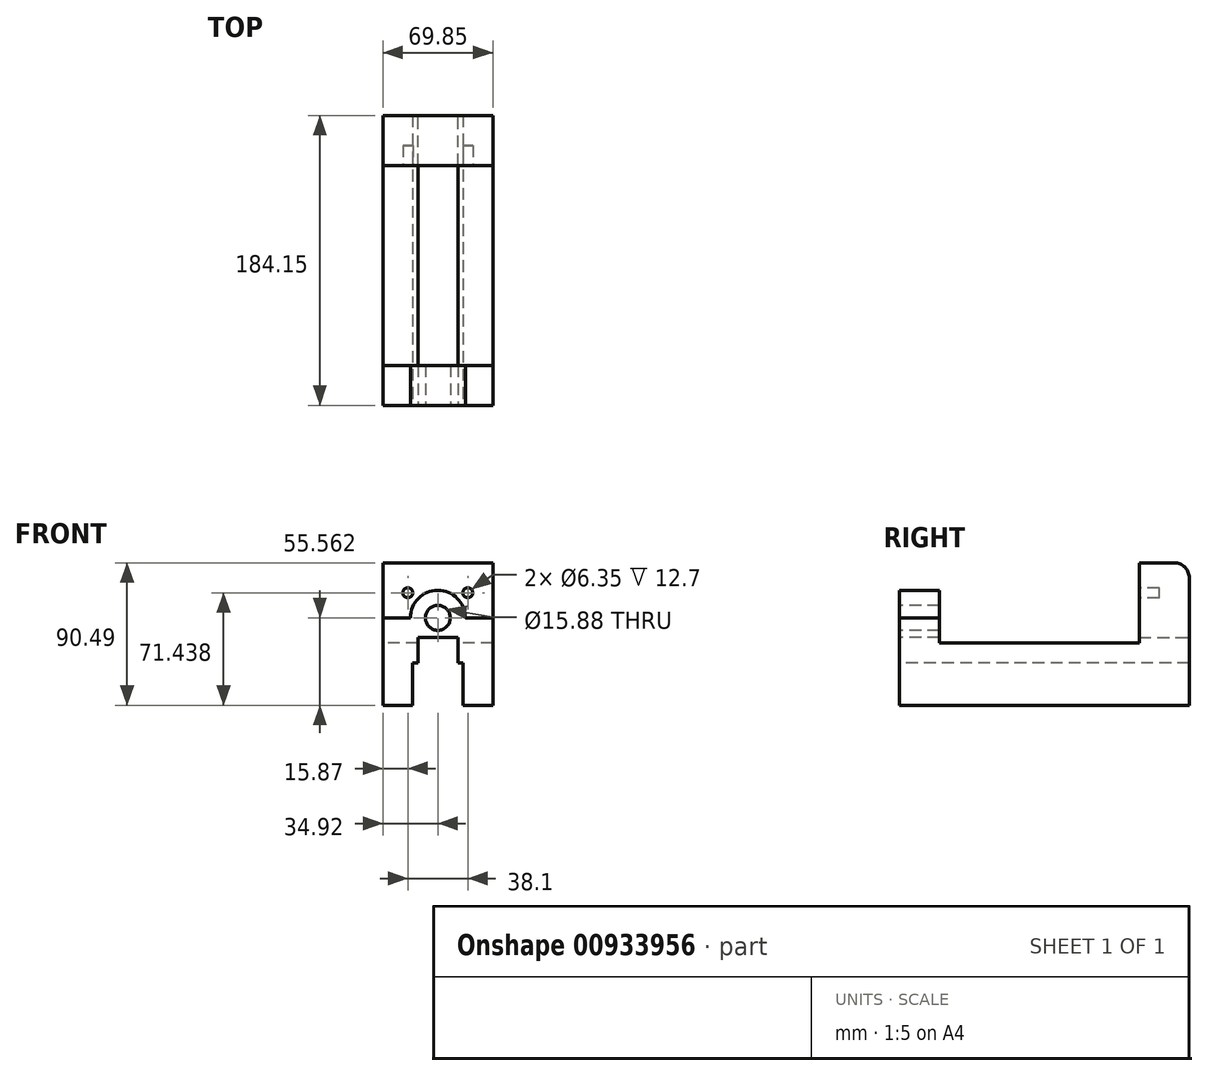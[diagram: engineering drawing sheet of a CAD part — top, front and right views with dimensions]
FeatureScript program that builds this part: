
annotation { "Feature Type Name" : "Feature", "Feature Type Description" : "" }
export const myFeature = defineFeature(function(context is Context, id is Id, definition is map)
    precondition{}
    {
        {
            var Q0;
            Q0=qCreatedBy(makeId("Front.planeOp"),FACE);
            var sketch = newSketch(context, id + "F0", { "sketchPlane" : qUnion([Q0])});
            skLineSegment(sketch, "E0", {"start": v(-27.11, 0) * mm, "end": v(42.74, 0) * mm});
            skLineSegment(sketch, "E1", {"start": v(42.74, 0) * mm, "end": v(42.74, 55.56) * mm});
            skLineSegment(sketch, "E2", {"start": v(42.74, 55.56) * mm, "end": v(-27.11, 55.56) * mm});
            skLineSegment(sketch, "E3", {"start": v(-27.11, 55.56) * mm, "end": v(-27.11, 0) * mm});
            skSolve(sketch);
        }
        {
            var Q0;
            Q0=makeQuery(id+"F0.imprint","IMPRINT",FACE,{"disambiguationData":[TD([[makeQuery(id+"F0.imprint","IMPRINT",EDGE,{"derivedFrom":sQuery(id+"F0.wireOp",EDGE,"E0")}),1.0]])]});
            extrude(context, id + "F1", {"entities" : qUnion([Q0]), "depth" : 25.4 * mm, "offsetDistance" : 25.4 * mm});
        }
        {
            var Q0;
            Q0=makeQuery(id+"F1.opExtrude","CAP_FACE",FACE,{"disambiguationData":[OSD([sQuery(id+"F0.wireOp",EDGE,"E0"),sQuery(id+"F0.wireOp",EDGE,"E1"),sQuery(id+"F0.wireOp",EDGE,"E2"),sQuery(id+"F0.wireOp",EDGE,"E3")])],"isStart":false});
            var sketch = newSketch(context, id + "F2", { "sketchPlane" : qUnion([Q0])});
            skCircle(sketch, "E4", {"center": v(7.81, 55.56) * mm, "radius": 17.46 * mm});
            skSolve(sketch);
        }
        {
            var Q0;
            {var subQ0=sQuery(id+"F2.wireOp",EDGE,"E4");var subQ1=makeQuery(id+"F1.opExtrude","CAP_EDGE",EDGE,{"disambiguationData":[OSD([sQuery(id+"F0.wireOp",EDGE,"E2")])],"isStart":false});var subQ2=makeQuery(id+"F2.imprint","INTERSECT",VERTEX,{"disambiguationData":[OD(0.0)],"derivedFrom":[subQ1,subQ0]});Q0=makeQuery(id+"F2.imprint","IMPRINT",FACE,{"disambiguationData":[TD([[makeQuery(id+"F2.imprint","IMPRINT",EDGE,{"disambiguationData":[TD([[subQ2,-1.0]])],"derivedFrom":subQ0}),1.0]])]});}
            extrude(context, id + "F3", {"entities" : qUnion([Q0]), "operationType" : NewBodyOperationType.ADD, "oppositeDirection" : true, "depth" : 25.4 * mm, "offsetDistance" : 25.4 * mm});
        }
        {
            var Q0;
            {var subQ0=sQuery(id+"F0.wireOp",EDGE,"E2");Q0=makeQuery(id+"F3.boolean.opBoolean","MERGE",FACE,{"derivedFrom":[makeQuery(id+"F1.opExtrude","CAP_FACE",FACE,{"disambiguationData":[OSD([sQuery(id+"F0.wireOp",EDGE,"E0"),sQuery(id+"F0.wireOp",EDGE,"E1"),subQ0,sQuery(id+"F0.wireOp",EDGE,"E3")])],"isStart":false}),makeQuery(id+"F3.opExtrude","CAP_FACE",FACE,{"disambiguationData":[OSD([subQ0,sQuery(id+"F2.wireOp",EDGE,"E4")])],"isStart":true})]});}
            var sketch = newSketch(context, id + "F4", { "sketchPlane" : qUnion([Q0])});
            skCircle(sketch, "E5", {"center": v(7.81, 55.56) * mm, "radius": 7.94 * mm});
            skSolve(sketch);
        }
        {
            var Q0;
            Q0=makeQuery(id+"F4.imprint","IMPRINT",FACE,{"disambiguationData":[TD([[makeQuery(id+"F4.imprint","IMPRINT",EDGE,{"derivedFrom":sQuery(id+"F4.wireOp",EDGE,"E5")}),1.0]])]});
            extrude(context, id + "F5", {"entities" : qUnion([Q0]), "operationType" : NewBodyOperationType.REMOVE, "oppositeDirection" : true, "depth" : 25.4 * mm, "offsetDistance" : 25.4 * mm});
        }
        {
            var Q0;
            {var subQ0=sQuery(id+"F0.wireOp",EDGE,"E2");Q0=makeQuery(id+"F3.boolean.opBoolean","MERGE",FACE,{"derivedFrom":[makeQuery(id+"F1.opExtrude","CAP_FACE",FACE,{"disambiguationData":[OSD([sQuery(id+"F0.wireOp",EDGE,"E0"),sQuery(id+"F0.wireOp",EDGE,"E1"),subQ0,sQuery(id+"F0.wireOp",EDGE,"E3")])],"isStart":true}),makeQuery(id+"F3.opExtrude","CAP_FACE",FACE,{"disambiguationData":[OSD([subQ0,sQuery(id+"F2.wireOp",EDGE,"E4")])],"isStart":false})]});}
            var sketch = newSketch(context, id + "F6", { "sketchPlane" : qUnion([Q0])});
            skLineSegment(sketch, "E6", {"start": v(-42.74, 0) * mm, "end": v(-42.74, 39.69) * mm});
            skLineSegment(sketch, "E7", {"start": v(-42.74, 39.69) * mm, "end": v(27.11, 39.69) * mm});
            skLineSegment(sketch, "E8", {"start": v(27.11, 39.69) * mm, "end": v(27.11, 0) * mm});
            skLineSegment(sketch, "E9", {"start": v(27.11, 0) * mm, "end": v(-42.74, 0) * mm});
            skSolve(sketch);
        }
        {
            var Q0;
            Q0=makeQuery(id+"F6.imprint","IMPRINT",FACE,{"disambiguationData":[TD([[makeQuery(id+"F6.imprint","IMPRINT",EDGE,{"derivedFrom":sQuery(id+"F6.wireOp",EDGE,"E6")}),-1.0]])]});
            extrude(context, id + "F7", {"entities" : qUnion([Q0]), "operationType" : NewBodyOperationType.ADD, "depth" : 127 * mm, "offsetDistance" : 25.4 * mm});
        }
        {
            var Q0;
            Q0=makeQuery(id+"F7.opExtrude","CAP_FACE",FACE,{"disambiguationData":[OSD([sQuery(id+"F6.wireOp",EDGE,"E6"),sQuery(id+"F6.wireOp",EDGE,"E7"),sQuery(id+"F6.wireOp",EDGE,"E8"),sQuery(id+"F6.wireOp",EDGE,"E9")])],"isStart":false});
            var sketch = newSketch(context, id + "F8", { "sketchPlane" : qUnion([Q0])});
            skLineSegment(sketch, "E10", {"start": v(-42.74, 0) * mm, "end": v(-42.74, 90.49) * mm});
            skLineSegment(sketch, "E11", {"start": v(-42.74, 90.49) * mm, "end": v(27.11, 90.49) * mm});
            skLineSegment(sketch, "E12", {"start": v(27.11, 90.49) * mm, "end": v(27.11, 0) * mm});
            skLineSegment(sketch, "E13", {"start": v(27.11, 0) * mm, "end": v(-42.74, 0) * mm});
            skSolve(sketch);
        }
        {
            var Q0;
            {var subQ2=sQuery(id+"F8.wireOp",EDGE,"E11");Q0=makeQuery(id+"F8.imprint","IMPRINT",FACE,{"disambiguationData":[TD([[makeQuery(id+"F8.imprint","IMPRINT",EDGE,{"derivedFrom":subQ2}),-1.0]])]});}
            var Q1;
            {var subQ0=sQuery(id+"F8.wireOp",EDGE,"E13");Q1=makeQuery(id+"F8.imprint","IMPRINT",FACE,{"disambiguationData":[TD([[makeQuery(id+"F8.imprint","IMPRINT",EDGE,{"derivedFrom":subQ0}),-1.0]])]});}
            extrude(context, id + "F9", {"entities" : qUnion([Q0, Q1]), "operationType" : NewBodyOperationType.ADD, "depth" : 31.75 * mm, "offsetDistance" : 25.4 * mm});
        }
        {
            var Q0;
            Q0=makeQuery(id+"F9.opExtrude","CAP_EDGE",EDGE,{"disambiguationData":[OSD([sQuery(id+"F8.wireOp",EDGE,"E11")])],"isStart":false});
            fillet(context, id + "F10", {"entities" : qUnion([Q0]), "radius" : 9.52 * mm, "tangentPropagation" : true, "allowEdgeOverflow" : false});
        }
        {
            var Q0;
            {var subQ0=sQuery(id+"F0.wireOp",EDGE,"E2");Q0=makeQuery(id+"F3.boolean.opBoolean","MERGE",FACE,{"derivedFrom":[makeQuery(id+"F1.opExtrude","CAP_FACE",FACE,{"disambiguationData":[OSD([sQuery(id+"F0.wireOp",EDGE,"E0"),sQuery(id+"F0.wireOp",EDGE,"E1"),subQ0,sQuery(id+"F0.wireOp",EDGE,"E3")])],"isStart":false}),makeQuery(id+"F3.opExtrude","CAP_FACE",FACE,{"disambiguationData":[OSD([subQ0,sQuery(id+"F2.wireOp",EDGE,"E4")])],"isStart":true})]});}
            var sketch = newSketch(context, id + "F11", { "sketchPlane" : qUnion([Q0])});
            skLineSegment(sketch, "E14", {"start": v(-27.11, 0) * mm, "end": v(-8.13, 0) * mm});
            skLineSegment(sketch, "E15", {"start": v(-8.13, 0) * mm, "end": v(-8.13, 26.99) * mm});
            skLineSegment(sketch, "E16", {"start": v(-8.13, 26.99) * mm, "end": v(23.75, 26.99) * mm});
            skLineSegment(sketch, "E17", {"start": v(23.75, 26.99) * mm, "end": v(23.75, 0) * mm});
            skLineSegment(sketch, "E18", {"start": v(23.75, 0) * mm, "end": v(-8.13, 0) * mm});
            skLineSegment(sketch, "E19", {"start": v(7.81, 0) * mm, "end": v(-4.89, 0) * mm});
            skLineSegment(sketch, "E20", {"start": v(-4.89, 0) * mm, "end": v(20.51, 0) * mm});
            skLineSegment(sketch, "E21", {"start": v(20.51, 0) * mm, "end": v(20.51, 26.99) * mm});
            skLineSegment(sketch, "E22", {"start": v(20.51, 26.99) * mm, "end": v(20.51, 39.64) * mm});
            skLineSegment(sketch, "E23", {"start": v(-4.89, 0) * mm, "end": v(-4.89, 26.99) * mm});
            skLineSegment(sketch, "E24", {"start": v(-4.89, 26.99) * mm, "end": v(-4.89, 39.64) * mm});
            skLineSegment(sketch, "E25", {"start": v(-4.89, 39.64) * mm, "end": v(20.51, 39.64) * mm});
            skSolve(sketch);
        }
        {
            var Q0;
            Q0=makeQuery(id+"F11.imprint","IMPRINT",FACE,{"disambiguationData":[TD([[makeQuery(id+"F11.imprint","IMPRINT",EDGE,{"derivedFrom":sQuery(id+"F11.wireOp",EDGE,"E14")}),1.0]])]});
            var sketch = newSketch(context, id + "F12", { "sketchPlane" : qUnion([Q0])});
            skLineSegment(sketch, "E26", {"start": v(-4.87, 27) * mm, "end": v(-4.87, 44.72) * mm});
            skLineSegment(sketch, "E27", {"start": v(-4.87, 27) * mm, "end": v(20.53, 27) * mm});
            skLineSegment(sketch, "E28", {"start": v(20.53, 27) * mm, "end": v(20.53, 44.72) * mm});
            skLineSegment(sketch, "E29", {"start": v(20.53, 44.72) * mm, "end": v(-4.87, 44.72) * mm});
            skSolve(sketch);
        }
        {
            var Q0;
            {var subQ1=sQuery(id+"F12.wireOp",EDGE,"E28");Q0=makeQuery(id+"F12.imprint","IMPRINT",FACE,{"disambiguationData":[TD([[makeQuery(id+"F12.imprint","IMPRINT",EDGE,{"derivedFrom":subQ1}),1.0]])]});}
            var Q1;
            {var subQ0=sQuery(id+"F12.wireOp",EDGE,"E27");var subQ1=sQuery(id+"F12.wireOp",EDGE,"E26");var subQ2=makeQuery(id+"F12.imprint","INTERSECT",VERTEX,{"derivedFrom":[subQ1,subQ0]});Q1=makeQuery(id+"F12.imprint","IMPRINT",FACE,{"disambiguationData":[TD([[makeQuery(id+"F12.imprint","IMPRINT",EDGE,{"disambiguationData":[TD([[subQ2,-1.0]])],"derivedFrom":subQ1}),-1.0]])]});}
            var Q2;
            {var subQ2=sQuery(id+"F11.wireOp",EDGE,"E21");Q2=makeQuery(id+"F11.imprint","IMPRINT",FACE,{"disambiguationData":[TD([[makeQuery(id+"F11.imprint","IMPRINT",EDGE,{"derivedFrom":subQ2}),1.0]])]});}
            var Q3;
            {var subQ0=sQuery(id+"F11.wireOp",EDGE,"E15");Q3=makeQuery(id+"F11.imprint","IMPRINT",FACE,{"disambiguationData":[TD([[makeQuery(id+"F11.imprint","IMPRINT",EDGE,{"derivedFrom":subQ0}),-1.0]])]});}
            var Q4;
            {var subQ0=sQuery(id+"F11.wireOp",EDGE,"E17");Q4=makeQuery(id+"F11.imprint","IMPRINT",FACE,{"disambiguationData":[TD([[makeQuery(id+"F11.imprint","IMPRINT",EDGE,{"derivedFrom":subQ0}),-1.0]])]});}
            extrude(context, id + "F13", {"entities" : qUnion([Q0, Q1, Q2, Q3, Q4]), "operationType" : NewBodyOperationType.REMOVE, "oppositeDirection" : true, "depth" : 210.3 * mm, "offsetDistance" : 25.4 * mm});
        }
        {
            var Q0;
            Q0=makeQuery(id+"F9.opExtrude","CAP_FACE",FACE,{"disambiguationData":[OSD([sQuery(id+"F8.wireOp",EDGE,"E10"),sQuery(id+"F8.wireOp",EDGE,"E11"),sQuery(id+"F8.wireOp",EDGE,"E12"),sQuery(id+"F8.wireOp",EDGE,"E13")])],"isStart":true});
            var sketch = newSketch(context, id + "F14", { "sketchPlane" : qUnion([Q0])});
            skLineSegment(sketch, "E30", {"start": v(-27.11, 90.49) * mm, "end": v(-11.24, 90.49) * mm});
            skLineSegment(sketch, "E31", {"start": v(-11.24, 90.49) * mm, "end": v(-11.24, 71.44) * mm});
            skCircle(sketch, "E32", {"center": v(-11.24, 71.44) * mm, "radius": 3.18 * mm});
            skLineSegment(sketch, "E33", {"start": v(-11.24, 90.49) * mm, "end": v(26.86, 90.49) * mm});
            skLineSegment(sketch, "E34", {"start": v(26.86, 90.49) * mm, "end": v(26.86, 71.44) * mm});
            skCircle(sketch, "E35", {"center": v(26.86, 71.44) * mm, "radius": 3.18 * mm});
            skSolve(sketch);
        }
        {
            var Q0;
            Q0=makeQuery(id+"F14.imprint","IMPRINT",FACE,{"disambiguationData":[TD([[makeQuery(id+"F14.imprint","IMPRINT",EDGE,{"derivedFrom":sQuery(id+"F14.wireOp",EDGE,"E32")}),1.0]])]});
            var Q1;
            Q1=makeQuery(id+"F14.imprint","IMPRINT",FACE,{"disambiguationData":[TD([[makeQuery(id+"F14.imprint","IMPRINT",EDGE,{"derivedFrom":sQuery(id+"F14.wireOp",EDGE,"E35")}),1.0]])]});
            extrude(context, id + "F15", {"entities" : qUnion([Q0, Q1]), "operationType" : NewBodyOperationType.REMOVE, "oppositeDirection" : true, "depth" : 12.7 * mm, "offsetDistance" : 25.4 * mm});
        }
        {
            var Q0;
            Q0=makeQuery(id+"F9.opExtrude","CAP_FACE",FACE,{"disambiguationData":[OSD([sQuery(id+"F8.wireOp",EDGE,"E10"),sQuery(id+"F8.wireOp",EDGE,"E11"),sQuery(id+"F8.wireOp",EDGE,"E12"),sQuery(id+"F8.wireOp",EDGE,"E13")])],"isStart":false});
            var sketch = newSketch(context, id + "F16", { "sketchPlane" : qUnion([Q0])});
            skLineSegment(sketch, "E36", {"start": v(-20.53, 44.72) * mm, "end": v(-20.53, 43.2) * mm});
            skLineSegment(sketch, "E37", {"start": v(-20.53, 43.2) * mm, "end": v(4.87, 43.2) * mm});
            skLineSegment(sketch, "E38", {"start": v(4.87, 43.2) * mm, "end": v(4.87, 44.72) * mm});
            skLineSegment(sketch, "E39", {"start": v(4.87, 44.72) * mm, "end": v(-20.53, 44.72) * mm});
            skSolve(sketch);
        }
        {
            var Q0;
            Q0=makeQuery(id+"F16.imprint","IMPRINT",FACE,{"disambiguationData":[TD([[makeQuery(id+"F16.imprint","IMPRINT",EDGE,{"derivedFrom":sQuery(id+"F16.wireOp",EDGE,"E36")}),1.0]])]});
            extrude(context, id + "F17", {"entities" : qUnion([Q0]), "operationType" : NewBodyOperationType.ADD, "oppositeDirection" : true, "depth" : 31.75 * mm, "offsetDistance" : 25.4 * mm});
        }
        {
            var Q0;
            {var subQ0=sQuery(id+"F0.wireOp",EDGE,"E2");Q0=makeQuery(id+"F3.boolean.opBoolean","MERGE",FACE,{"derivedFrom":[makeQuery(id+"F1.opExtrude","CAP_FACE",FACE,{"disambiguationData":[OSD([sQuery(id+"F0.wireOp",EDGE,"E0"),sQuery(id+"F0.wireOp",EDGE,"E1"),subQ0,sQuery(id+"F0.wireOp",EDGE,"E3")])],"isStart":false}),makeQuery(id+"F3.opExtrude","CAP_FACE",FACE,{"disambiguationData":[OSD([subQ0,sQuery(id+"F2.wireOp",EDGE,"E4")])],"isStart":true})]});}
            var sketch = newSketch(context, id + "F18", { "sketchPlane" : qUnion([Q0])});
            skLineSegment(sketch, "E40", {"start": v(-4.87, 44.72) * mm, "end": v(-4.87, 43.2) * mm});
            skLineSegment(sketch, "E41", {"start": v(-4.87, 43.2) * mm, "end": v(20.53, 43.2) * mm});
            skLineSegment(sketch, "E42", {"start": v(20.53, 43.2) * mm, "end": v(20.53, 44.72) * mm});
            skLineSegment(sketch, "E43", {"start": v(20.53, 44.72) * mm, "end": v(-4.87, 44.72) * mm});
            skSolve(sketch);
        }
        {
            var Q0;
            Q0=makeQuery(id+"F18.imprint","IMPRINT",FACE,{"disambiguationData":[TD([[makeQuery(id+"F18.imprint","IMPRINT",EDGE,{"derivedFrom":sQuery(id+"F18.wireOp",EDGE,"E40")}),-1.0]])]});
            extrude(context, id + "F19", {"entities" : qUnion([Q0]), "operationType" : NewBodyOperationType.ADD, "oppositeDirection" : true, "depth" : 25.4 * mm, "offsetDistance" : 25.4 * mm});
        }
    });
